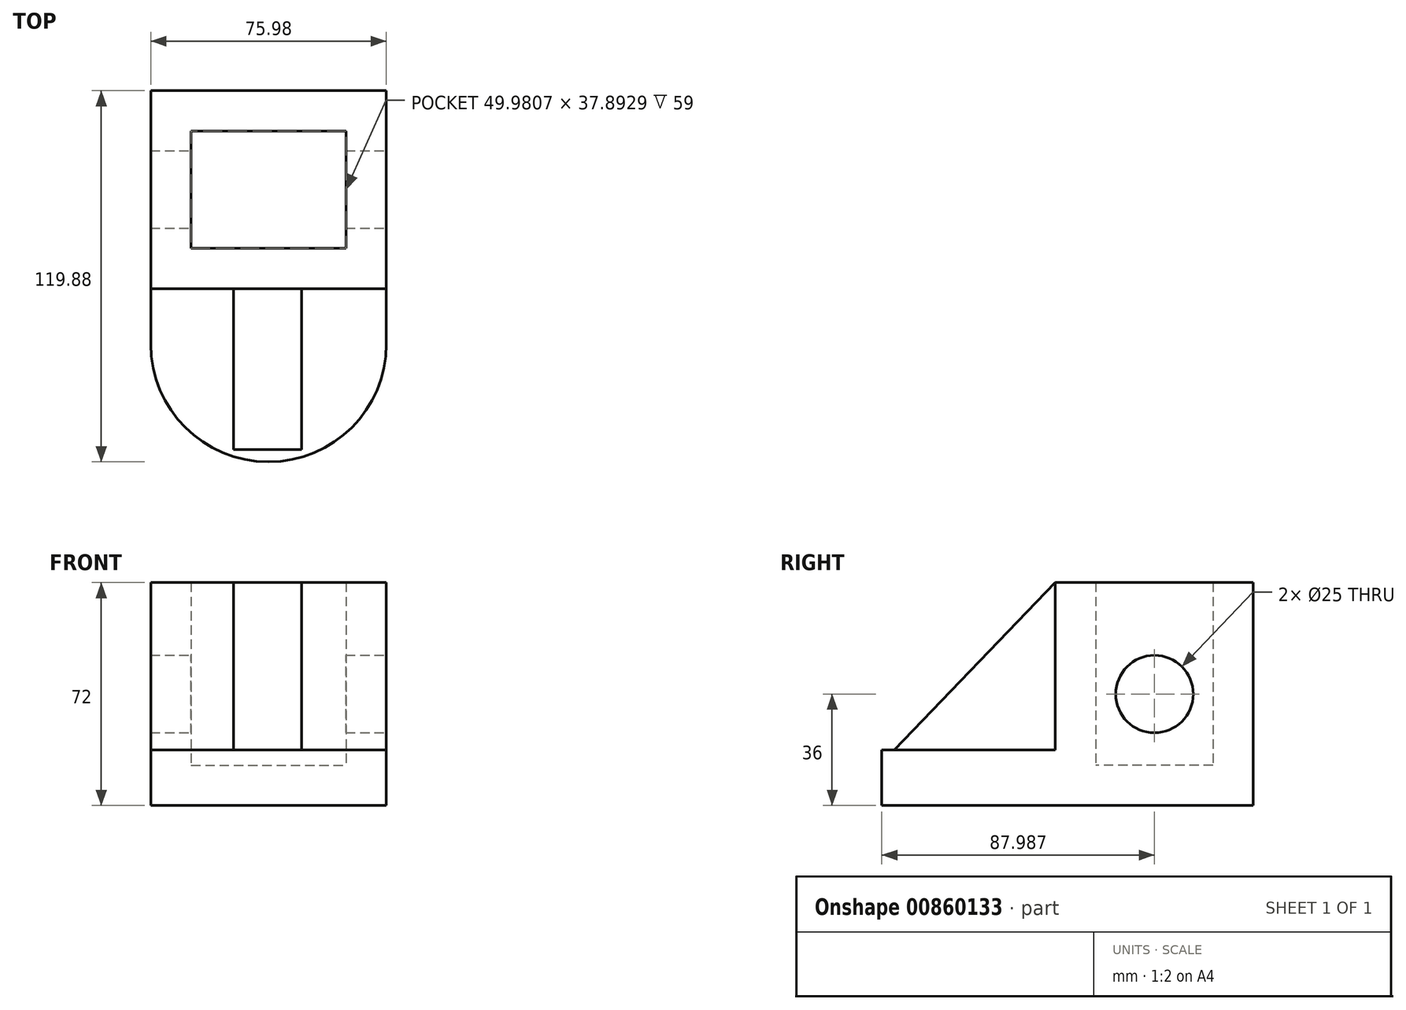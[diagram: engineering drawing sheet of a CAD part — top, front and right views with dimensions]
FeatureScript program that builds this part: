
annotation { "Feature Type Name" : "Feature", "Feature Type Description" : "" }
export const myFeature = defineFeature(function(context is Context, id is Id, definition is map)
    precondition{}
    {
        {
            var Q0;
            Q0=qCreatedBy(makeId("Top.planeOp"),FACE);
            var sketch = newSketch(context, id + "F0", { "sketchPlane" : qUnion([Q0])});
            skLineSegment(sketch, "E0.bottom", {"start": v(-38.7, 24.32) * mm, "end": v(37.27, 24.32) * mm});
            skLineSegment(sketch, "E0.top", {"start": v(-38.7, -39.57) * mm, "end": v(37.27, -39.57) * mm});
            skLineSegment(sketch, "E0.left", {"start": v(-38.7, 24.32) * mm, "end": v(-38.7, -39.57) * mm});
            skLineSegment(sketch, "E0.right", {"start": v(37.27, 24.32) * mm, "end": v(37.27, -39.57) * mm});
            skLineSegment(sketch, "E1", {"start": v(-38.7, -39.57) * mm, "end": v(-38.7, -95.52) * mm});
            skLineSegment(sketch, "E2", {"start": v(-38.7, -95.52) * mm, "end": v(37.47, -95.52) * mm});
            skLineSegment(sketch, "E3", {"start": v(37.47, -95.52) * mm, "end": v(37.27, -39.57) * mm});
            skSolve(sketch);
        }
        {
            var Q0;
            Q0=makeQuery(id+"F0.imprint","IMPRINT",FACE,{"disambiguationData":[TD([[makeQuery(id+"F0.imprint","IMPRINT",EDGE,{"derivedFrom":sQuery(id+"F0.wireOp",EDGE,"E0.bottom")}),-1.0]])]});
            extrude(context, id + "F1", {"entities" : qUnion([Q0]), "depth" : 72 * mm, "offsetDistance" : 25 * mm});
        }
        {
            var Q0;
            Q0=makeQuery(id+"F1.opExtrude","CAP_FACE",FACE,{"disambiguationData":[OSD([sQuery(id+"F0.wireOp",EDGE,"E0.bottom"),sQuery(id+"F0.wireOp",EDGE,"E0.top"),sQuery(id+"F0.wireOp",EDGE,"E0.left"),sQuery(id+"F0.wireOp",EDGE,"E0.right")])],"isStart":false});
            shell(context, id + "F2", {"entities" : qUnion([Q0]), "thickness" : 13 * mm});
        }
        {
            var Q0;
            Q0=makeQuery(id+"F1.opExtrude","SWEPT_FACE",FACE,{"disambiguationData":[OSD([sQuery(id+"F0.wireOp",EDGE,"E0.right")])]});
            var sketch = newSketch(context, id + "F3", { "sketchPlane" : qUnion([Q0])});
            skCircle(sketch, "E4", {"center": v(-7.57, 36) * mm, "radius": 12.5 * mm});
            skSolve(sketch);
        }
        {
            var Q0;
            Q0=makeQuery(id+"F3.imprint","IMPRINT",FACE,{"disambiguationData":[TD([[makeQuery(id+"F3.imprint","IMPRINT",EDGE,{"derivedFrom":sQuery(id+"F3.wireOp",EDGE,"E4")}),1.0]])]});
            extrude(context, id + "F4", {"entities" : qUnion([Q0]), "operationType" : NewBodyOperationType.REMOVE, "oppositeDirection" : true, "depth" : 100 * mm, "offsetDistance" : 25 * mm});
        }
        {
            var Q0;
            Q0=makeQuery(id+"F1.opExtrude","SWEPT_FACE",FACE,{"disambiguationData":[OSD([sQuery(id+"F0.wireOp",EDGE,"E0.top")])]});
            var sketch = newSketch(context, id + "F5", { "sketchPlane" : qUnion([Q0])});
            skLineSegment(sketch, "E5", {"start": v(37.27, 0) * mm, "end": v(37.27, 18) * mm});
            skLineSegment(sketch, "E6", {"start": v(37.27, 18) * mm, "end": v(-38.7, 18) * mm});
            skLineSegment(sketch, "E7", {"start": v(-38.7, 18) * mm, "end": v(-38.7, 0) * mm});
            skLineSegment(sketch, "E8", {"start": v(-38.7, 0) * mm, "end": v(37.27, 0) * mm});
            skLineSegment(sketch, "E9", {"start": v(-38.7, 72) * mm, "end": v(-0.72, 72) * mm});
            skLineSegment(sketch, "E10", {"start": v(-11.72, 18) * mm, "end": v(-11.72, 72) * mm});
            skLineSegment(sketch, "E11", {"start": v(-11.72, 72) * mm, "end": v(10.28, 72) * mm});
            skLineSegment(sketch, "E12", {"start": v(10.28, 72) * mm, "end": v(10.28, 18) * mm});
            skLineSegment(sketch, "E13", {"start": v(-11.72, 18) * mm, "end": v(10.28, 18) * mm});
            skSolve(sketch);
        }
        {
            var Q0;
            Q0=makeQuery(id+"F5.imprint","IMPRINT",FACE,{"disambiguationData":[TD([[makeQuery(id+"F5.imprint","IMPRINT",EDGE,{"derivedFrom":sQuery(id+"F5.wireOp",EDGE,"E5")}),-1.0]])]});
            extrude(context, id + "F6", {"entities" : qUnion([Q0]), "operationType" : NewBodyOperationType.ADD, "depth" : 56 * mm, "offsetDistance" : 25 * mm});
        }
        {
            var Q0;
            Q0=makeQuery(id+"F1.opExtrude","SWEPT_FACE",FACE,{"disambiguationData":[OSD([sQuery(id+"F0.wireOp",EDGE,"E0.top")])]});
            var sketch = newSketch(context, id + "F7", { "sketchPlane" : qUnion([Q0])});
            skLineSegment(sketch, "E14", {"start": v(-38.7, 72) * mm, "end": v(-0.7, 72) * mm});
            skLineSegment(sketch, "E15", {"start": v(-12.1, 18) * mm, "end": v(-12.1, 72) * mm});
            skLineSegment(sketch, "E16", {"start": v(9.9, 72) * mm, "end": v(9.9, 18) * mm});
            skLineSegment(sketch, "E17", {"start": v(-12.1, 18) * mm, "end": v(9.9, 18) * mm});
            skSolve(sketch);
        }
        {
            var Q0;
            {var subQ1=sQuery(id+"F7.wireOp",EDGE,"E15");Q0=makeQuery(id+"F7.imprint","IMPRINT",FACE,{"disambiguationData":[TD([[makeQuery(id+"F7.imprint","IMPRINT",EDGE,{"derivedFrom":subQ1}),-1.0]])]});}
            extrude(context, id + "F8", {"entities" : qUnion([Q0]), "operationType" : NewBodyOperationType.ADD, "depth" : 52 * mm, "offsetDistance" : 25 * mm});
        }
        {
            var Q0;
            Q0=makeQuery(id+"F8.opExtrude","SWEPT_FACE",FACE,{"disambiguationData":[OSD([sQuery(id+"F7.wireOp",EDGE,"E16")])]});
            var sketch = newSketch(context, id + "F9", { "sketchPlane" : qUnion([Q0])});
            skLineSegment(sketch, "E18", {"start": v(-91.57, 18) * mm, "end": v(-39.57, 72) * mm});
            skSolve(sketch);
        }
        {
            var Q0;
            Q0=makeQuery(id+"F9.imprint","IMPRINT",FACE,{"disambiguationData":[TD([[makeQuery(id+"F9.imprint","IMPRINT",EDGE,{"derivedFrom":sQuery(id+"F9.wireOp",EDGE,"E18")}),1.0]])]});
            extrude(context, id + "F10", {"entities" : qUnion([Q0]), "operationType" : NewBodyOperationType.REMOVE, "oppositeDirection" : true, "depth" : 25 * mm, "offsetDistance" : 25 * mm});
        }
        {
            var Q0;
            Q0=makeQuery(id+"F6.opExtrude","SWEPT_FACE",FACE,{"disambiguationData":[OSD([sQuery(id+"F5.wireOp",EDGE,"E6"),sQuery(id+"F5.wireOp",EDGE,"E13")])]});
            var sketch = newSketch(context, id + "F11", { "sketchPlane" : qUnion([Q0])});
            skArc(sketch, "E19", {"start": v(-38.7, -57.57) * mm, "mid": v(-0.72, -95.56) * mm, "end": v(37.27, -57.57) * mm});
            skSolve(sketch);
        }
        {
            var Q0;
            {var subQ0=sQuery(id+"F11.wireOp",EDGE,"E19");Q0=makeQuery(id+"F11.imprint","IMPRINT",FACE,{"disambiguationData":[TD([[makeQuery(id+"F11.imprint","IMPRINT",EDGE,{"derivedFrom":subQ0}),-1.0]])]});}
            extrude(context, id + "F12", {"entities" : qUnion([Q0]), "operationType" : NewBodyOperationType.REMOVE, "oppositeDirection" : true, "depth" : 25 * mm, "offsetDistance" : 25 * mm});
        }
    });
